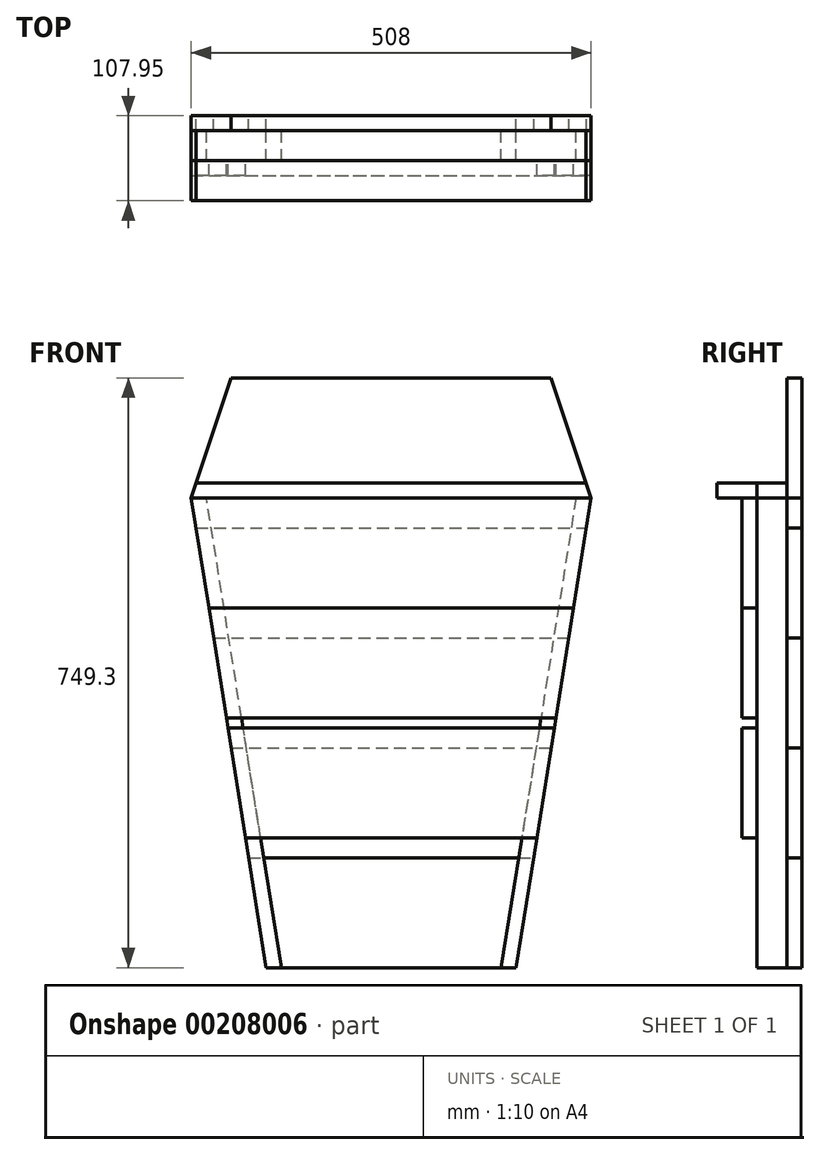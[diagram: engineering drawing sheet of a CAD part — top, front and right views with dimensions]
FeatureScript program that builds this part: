
annotation { "Feature Type Name" : "Feature", "Feature Type Description" : "" }
export const myFeature = defineFeature(function(context is Context, id is Id, definition is map)
    precondition{}
    {
        {
            var Q0;
            Q0=qCreatedBy(makeId("Front.planeOp"),FACE);
            var sketch = newSketch(context, id + "F0", { "sketchPlane" : qUnion([Q0])});
            skLineSegment(sketch, "E0", {"start": v(0, 0) * mm, "end": v(0, -749.3) * mm, "construction": true});
            skLineSegment(sketch, "E1", {"start": v(-203.2, 0) * mm, "end": v(203.2, 0) * mm});
            skLineSegment(sketch, "E2", {"start": v(203.2, 0) * mm, "end": v(254, -152.4) * mm});
            skLineSegment(sketch, "E3", {"start": v(254, -152.4) * mm, "end": v(158.75, -749.3) * mm});
            skLineSegment(sketch, "E4", {"start": v(158.75, -749.3) * mm, "end": v(-158.75, -749.3) * mm});
            skLineSegment(sketch, "E5", {"start": v(-158.75, -749.3) * mm, "end": v(-254, -152.4) * mm});
            skLineSegment(sketch, "E6", {"start": v(-254, -152.4) * mm, "end": v(-203.2, 0) * mm});
            skSolve(sketch);
        }
        {
            var Q0;
            Q0=qCreatedBy(makeId("Front.planeOp"),FACE);
            var sketch = newSketch(context, id + "F1", { "sketchPlane" : qUnion([Q0])});
            skLineSegment(sketch, "E7.0", {"start": v(-158.75, -749.3) * mm, "end": v(-254, -152.4) * mm});
            skLineSegment(sketch, "E8.0", {"start": v(-254, -152.4) * mm, "end": v(-203.2, 0) * mm});
            skLineSegment(sketch, "E8.1", {"start": v(-203.2, 0) * mm, "end": v(203.2, 0) * mm});
            skLineSegment(sketch, "E8.2", {"start": v(203.2, 0) * mm, "end": v(254, -152.4) * mm});
            skLineSegment(sketch, "E8.3", {"start": v(254, -152.4) * mm, "end": v(158.75, -749.3) * mm});
            skLineSegment(sketch, "E9", {"start": v(-266.7, -190.5) * mm, "end": v(266.7, -190.5) * mm});
            skLineSegment(sketch, "E10", {"start": v(-225.63, -330.2) * mm, "end": v(225.63, -330.2) * mm});
            skLineSegment(sketch, "E11", {"start": v(-203.34, -469.9) * mm, "end": v(203.34, -469.9) * mm});
            skLineSegment(sketch, "E12", {"start": v(-181.04, -609.6) * mm, "end": v(181.04, -609.6) * mm});
            skLineSegment(sketch, "E13", {"start": v(-158.75, -749.3) * mm, "end": v(158.75, -749.3) * mm});
            skSolve(sketch);
        }
        {
            var Q0;
            {var subQ0=sQuery(id+"F1.wireOp",EDGE,"E11");Q0=makeQuery(id+"F1.imprint","IMPRINT",FACE,{"disambiguationData":[TD([[makeQuery(id+"F1.imprint","IMPRINT",EDGE,{"derivedFrom":subQ0}),-1.0]])]});}
            var Q1;
            {var subQ7=sQuery(id+"F1.wireOp",EDGE,"E9");Q1=makeQuery(id+"F1.imprint","IMPRINT",FACE,{"disambiguationData":[TD([[makeQuery(id+"F1.imprint","IMPRINT",EDGE,{"derivedFrom":subQ7}),-1.0]])]});}
            extrude(context, id + "F2", {"entities" : qUnion([Q0, Q1]), "depth" : 19.05 * mm});
        }
        {
            var Q0;
            {var subQ0=sQuery(id+"F1.wireOp",EDGE,"E12");Q0=makeQuery(id+"F1.imprint","IMPRINT",FACE,{"disambiguationData":[TD([[makeQuery(id+"F1.imprint","IMPRINT",EDGE,{"derivedFrom":subQ0}),-1.0]])]});}
            var Q1;
            {var subQ0=sQuery(id+"F1.wireOp",EDGE,"E10");Q1=makeQuery(id+"F1.imprint","IMPRINT",FACE,{"disambiguationData":[TD([[makeQuery(id+"F1.imprint","IMPRINT",EDGE,{"derivedFrom":subQ0}),-1.0]])]});}
            var Q2;
            {var subQ0=sQuery(id+"F1.wireOp",EDGE,"E8.1");Q2=makeQuery(id+"F1.imprint","IMPRINT",FACE,{"disambiguationData":[TD([[makeQuery(id+"F1.imprint","IMPRINT",EDGE,{"derivedFrom":subQ0}),-1.0]])]});}
            extrude(context, id + "F3", {"entities" : qUnion([Q0, Q1, Q2]), "depth" : 19.05 * mm});
        }
        {
            var Q0;
            Q0=makeQuery(id+"F3.opExtrude","CAP_FACE",FACE,{"disambiguationData":[OSD([sQuery(id+"F1.wireOp",EDGE,"E8.0"),sQuery(id+"F1.wireOp",EDGE,"E8.1"),sQuery(id+"F1.wireOp",EDGE,"E8.2"),sQuery(id+"F1.wireOp",EDGE,"E9")])],"isStart":false});
            var sketch = newSketch(context, id + "F4", { "sketchPlane" : qUnion([Q0])});
            skLineSegment(sketch, "E14.0", {"start": v(-158.75, -749.3) * mm, "end": v(-254, -152.4) * mm});
            skLineSegment(sketch, "E14.1", {"start": v(-254, -152.4) * mm, "end": v(-247.65, -133.35) * mm});
            skLineSegment(sketch, "E14.3", {"start": v(247.65, -133.35) * mm, "end": v(254, -152.4) * mm});
            skLineSegment(sketch, "E14.4", {"start": v(254, -152.4) * mm, "end": v(158.75, -749.3) * mm});
            skLineSegment(sketch, "E14.9", {"start": v(-158.75, -749.3) * mm, "end": v(-139.46, -749.3) * mm});
            skLineSegment(sketch, "E15.0", {"start": v(-139.46, -749.3) * mm, "end": v(-234.7, -152.4) * mm});
            skLineSegment(sketch, "E16.0", {"start": v(-254, -152.4) * mm, "end": v(254, -152.4) * mm});
            skLineSegment(sketch, "E17.0", {"start": v(234.7, -152.4) * mm, "end": v(139.46, -749.3) * mm});
            skLineSegment(sketch, "E18.trimOffspring", {"start": v(139.46, -749.3) * mm, "end": v(158.75, -749.3) * mm});
            skLineSegment(sketch, "E19", {"start": v(-247.65, -133.35) * mm, "end": v(247.65, -133.35) * mm});
            skPoint(sketch, "E20.orphan", {"position": v(-203.2, 0) * mm});
            skPoint(sketch, "E21.orphan", {"position": v(203.2, 0) * mm});
            skSolve(sketch);
        }
        {
            var Q0;
            {var subQ0=sQuery(id+"F4.wireOp",EDGE,"E14.1");var subQ1=makeQuery(id+"F3.opExtrude","CAP_EDGE",EDGE,{"disambiguationData":[OSD([sQuery(id+"F1.wireOp",EDGE,"E9")])],"isStart":false});var subQ2=makeQuery(id+"F4.imprint","INTERSECT",VERTEX,{"derivedFrom":[subQ1,subQ0]});Q0=makeQuery(id+"F4.imprint","IMPRINT",FACE,{"disambiguationData":[TD([[makeQuery(id+"F4.imprint","IMPRINT",EDGE,{"disambiguationData":[TD([[subQ2,-1.0]])],"derivedFrom":subQ0}),-1.0]])]});}
            var Q1;
            {var subQ3=sQuery(id+"F4.wireOp",EDGE,"EgI6hWIt-TqMT-mpfX-QcLF-RLHUQHIuj730");Q1=makeQuery(id+"F4.imprint","IMPRINT",FACE,{"disambiguationData":[TD([[makeQuery(id+"F4.imprint","IMPRINT",EDGE,{"derivedFrom":subQ3}),1.0]])]});}
            var Q2;
            {var subQ0=sQuery(id+"F4.wireOp",EDGE,"E14.3");var subQ1=makeQuery(id+"F3.opExtrude","CAP_EDGE",EDGE,{"disambiguationData":[OSD([sQuery(id+"F1.wireOp",EDGE,"E9")])],"isStart":false});var subQ2=makeQuery(id+"F4.imprint","INTERSECT",VERTEX,{"derivedFrom":[subQ1,subQ0]});Q2=makeQuery(id+"F4.imprint","IMPRINT",FACE,{"disambiguationData":[TD([[makeQuery(id+"F4.imprint","IMPRINT",EDGE,{"disambiguationData":[TD([[subQ2,1.0]])],"derivedFrom":subQ0}),-1.0]])]});}
            var Q3;
            {var subQ3=sQuery(id+"F4.wireOp",EDGE,"bw0RLSld-EMCl-pPfj-AZWv-z4aP7sGst2gz");Q3=makeQuery(id+"F4.imprint","IMPRINT",FACE,{"disambiguationData":[TD([[makeQuery(id+"F4.imprint","IMPRINT",EDGE,{"derivedFrom":subQ3}),1.0]])]});}
            extrude(context, id + "F5", {"entities" : qUnion([Q0, Q1, Q2, Q3]), "depth" : 38.1 * mm});
        }
        {
            var Q0;
            {var subQ0=sQuery(id+"F4.wireOp",EDGE,"E14.2");Q0=makeQuery(id+"F4.imprint","IMPRINT",FACE,{"disambiguationData":[TD([[makeQuery(id+"F4.imprint","IMPRINT",EDGE,{"derivedFrom":subQ0}),-1.0]])]});}
            var Q1;
            Q1=makeQuery(id+"F4.imprint","IMPRINT",FACE,{"disambiguationData":[TD([[makeQuery(id+"F4.imprint","IMPRINT",EDGE,{"derivedFrom":sQuery(id+"F4.wireOp",EDGE,"E14.0")}),-1.0]])]});
            var Q2;
            Q2=makeQuery(id+"F4.imprint","IMPRINT",FACE,{"disambiguationData":[TD([[makeQuery(id+"F4.imprint","IMPRINT",EDGE,{"derivedFrom":sQuery(id+"F4.wireOp",EDGE,"E14.4")}),-1.0]])]});
            extrude(context, id + "F6", {"entities" : qUnion([Q0, Q1, Q2]), "depth" : 38.1 * mm});
        }
        {
            var Q0;
            {var subQ4=sQuery(id+"F4.wireOp",EDGE,"E19");Q0=makeQuery(id+"F4.imprint","IMPRINT",FACE,{"disambiguationData":[TD([[makeQuery(id+"F4.imprint","IMPRINT",EDGE,{"derivedFrom":subQ4}),-1.0]])]});}
            extrude(context, id + "F7", {"entities" : qUnion([Q0]), "depth" : 88.9 * mm});
        }
        {
            var Q0;
            Q0=makeQuery(id+"F5.opExtrude","CAP_FACE",FACE,{"disambiguationData":[OSD([sQuery(id+"F4.wireOp",EDGE,"E14.3"),sQuery(id+"F4.wireOp",EDGE,"E16.0"),sQuery(id+"F4.wireOp",EDGE,"75e69c80-2e2e-43b6-884d-1c82ad79f3f1.0"),sQuery(id+"F4.wireOp",EDGE,"bw0RLSld-EMCl-pPfj-AZWv-z4aP7sGst2gz")])],"isStart":false});
            var sketch = newSketch(context, id + "F8", { "sketchPlane" : qUnion([Q0])});
            skLineSegment(sketch, "E22.0", {"start": v(-254, -152.4) * mm, "end": v(254, -152.4) * mm});
            skLineSegment(sketch, "E23", {"start": v(-231.7, -292.1) * mm, "end": v(231.7, -292.1) * mm});
            skLineSegment(sketch, "E24", {"start": v(-209.41, -431.8) * mm, "end": v(209.41, -431.8) * mm});
            skLineSegment(sketch, "E25", {"start": v(-207.39, -444.5) * mm, "end": v(207.39, -444.5) * mm});
            skLineSegment(sketch, "E26", {"start": v(-185.1, -584.2) * mm, "end": v(185.1, -584.2) * mm});
            skLineSegment(sketch, "E27.0", {"start": v(-254, -152.4) * mm, "end": v(-254, -152.4) * mm});
            skLineSegment(sketch, "E27.1", {"start": v(-158.75, -749.3) * mm, "end": v(-254, -152.4) * mm});
            skLineSegment(sketch, "E27.2", {"start": v(254, -152.4) * mm, "end": v(254, -152.4) * mm});
            skLineSegment(sketch, "E27.3", {"start": v(254, -152.4) * mm, "end": v(158.75, -749.3) * mm});
            skSolve(sketch);
        }
        {
            var Q0;
            {var subQ1=sQuery(id+"F8.wireOp",EDGE,"E23");Q0=makeQuery(id+"F8.imprint","IMPRINT",FACE,{"disambiguationData":[TD([[makeQuery(id+"F8.imprint","IMPRINT",EDGE,{"derivedFrom":subQ1}),1.0]])]});}
            var Q1;
            {var subQ0=sQuery(id+"F8.wireOp",EDGE,"E25");Q1=makeQuery(id+"F8.imprint","IMPRINT",FACE,{"disambiguationData":[TD([[makeQuery(id+"F8.imprint","IMPRINT",EDGE,{"derivedFrom":subQ0}),-1.0]])]});}
            var Q2;
            {var subQ0=sQuery(id+"F8.wireOp",EDGE,"E27.2");Q2=makeQuery(id+"F8.imprint","IMPRINT",FACE,{"disambiguationData":[TD([[makeQuery(id+"F8.imprint","IMPRINT",EDGE,{"derivedFrom":subQ0}),-1.0]])]});}
            extrude(context, id + "F9", {"entities" : qUnion([Q0, Q1, Q2]), "depth" : 19.05 * mm});
        }
        {
            var Q0;
            {var subQ0=sQuery(id+"F8.wireOp",EDGE,"E23");Q0=makeQuery(id+"F8.imprint","IMPRINT",FACE,{"disambiguationData":[TD([[makeQuery(id+"F8.imprint","IMPRINT",EDGE,{"derivedFrom":subQ0}),-1.0]])]});}
            extrude(context, id + "F10", {"entities" : qUnion([Q0]), "depth" : 19.05 * mm});
        }
    });
